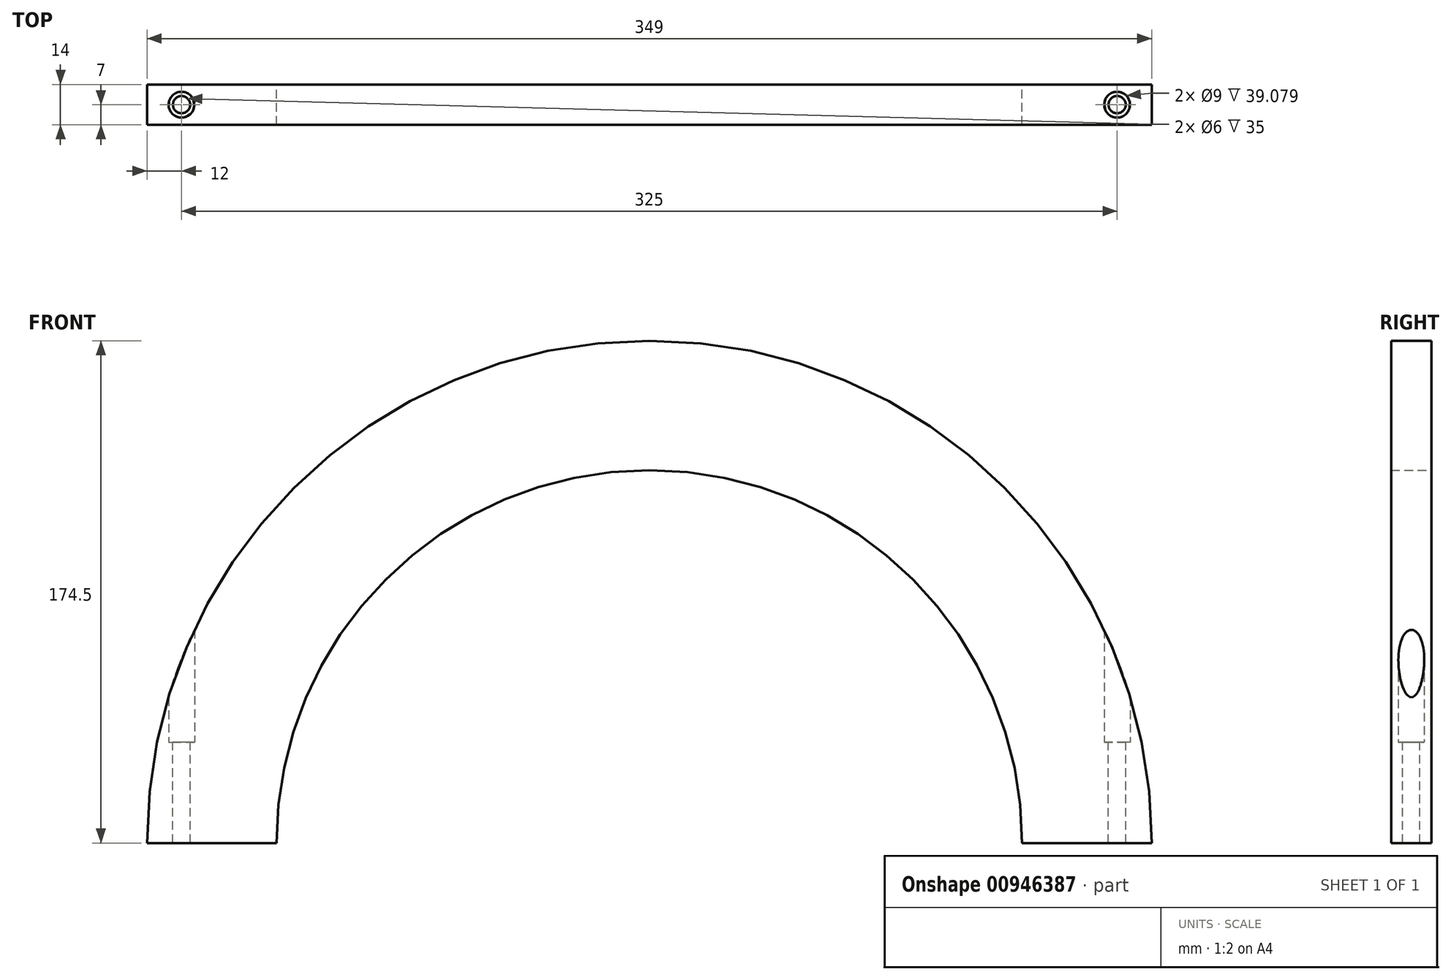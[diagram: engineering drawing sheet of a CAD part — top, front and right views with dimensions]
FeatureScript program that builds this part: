
annotation { "Feature Type Name" : "Feature", "Feature Type Description" : "" }
export const myFeature = defineFeature(function(context is Context, id is Id, definition is map)
    precondition{}
    {
        {
            var Q0;
            Q0=qCreatedBy(makeId("Front.planeOp"),FACE);
            var sketch = newSketch(context, id + "F0", { "sketchPlane" : qUnion([Q0])});
            skArc(sketch, "E0", {"start": v(174.5, 0) * mm, "mid": v(0, 174.5) * mm, "end": v(-174.5, 0) * mm});
            skArc(sketch, "E1", {"start": v(129.5, 0) * mm, "mid": v(0, 129.5) * mm, "end": v(-129.5, 0) * mm});
            skLineSegment(sketch, "E2", {"start": v(-174.5, 0) * mm, "end": v(-129.5, 0) * mm});
            skLineSegment(sketch, "E3.trimOffspring", {"start": v(129.5, 0) * mm, "end": v(174.5, 0) * mm});
            skLineSegment(sketch, "E4", {"start": v(-174.5, 0) * mm, "end": v(-174.5, -52.73) * mm, "construction": true});
            skLineSegment(sketch, "E5", {"start": v(0, 82.24) * mm, "end": v(0, -91.49) * mm, "construction": true});
            skPoint(sketch, "E6.MirrorCS.start.orphan", {"position": v(-174.5, 0) * mm});
            skSolve(sketch);
        }
        {
            var Q0;
            Q0=qSketchRegion(id+"F0",true);
            extrude(context, id + "F1", {"entities" : qUnion([Q0]), "endBound" : BoundingType.SYMMETRIC, "depth" : 14 * mm, "offsetDistance" : 25 * mm});
        }
        {
            var Q0;
            Q0=qSketchRegion(id+"F0",true);
            extrude(context, id + "F2", {"entities" : qUnion([Q0]), "operationType" : NewBodyOperationType.ADD, "endBound" : BoundingType.SYMMETRIC, "depth" : 12 * mm, "offsetDistance" : 25 * mm});
        }
        {
            var Q0;
            Q0=qCreatedBy(makeId("Top.planeOp"),FACE);
            cPlane(context, id + "F3", {"entities" : qUnion([Q0]), "cplaneType" : CPlaneType.OFFSET, "offset" : 55 * mm, "width" : 150 * mm, "height" : 150 * mm});
        }
        {
            var Q0;
            Q0=qCreatedBy(id+"F3.planeOp",FACE);
            var sketch = newSketch(context, id + "F4", { "sketchPlane" : qUnion([Q0])});
            skPoint(sketch, "E7.middle", {"position": v(-162.5, 0) * mm});
            skCircle(sketch, "E8", {"center": v(-162.5, 0) * mm, "radius": 4.5 * mm});
            skLineSegment(sketch, "E9", {"start": v(0, 45.88) * mm, "end": v(0, -42.52) * mm, "construction": true});
            skCircle(sketch, "E10.MirrorC", {"center": v(162.5, 0) * mm, "radius": 4.5 * mm});
            skSolve(sketch);
        }
        {
            var Q0;
            Q0 = qSketchRegion(id + "F4", true);
            extrude(context, id + "F5", {"entities" : qUnion([Q0]), "operationType" : NewBodyOperationType.REMOVE, "endBound" : BoundingType.THROUGH_ALL, "depth" : 25 * mm, "offsetDistance" : 25 * mm});
        }
        {
            var Q0;
            Q0 = qSketchRegion(id + "F4", true);
            extrude(context, id + "F6", {"entities" : qUnion([Q0]), "operationType" : NewBodyOperationType.REMOVE, "oppositeDirection" : true, "depth" : 20 * mm, "offsetDistance" : 25 * mm});
        }
        {
            var Q0;
            Q0=makeQuery(id+"F6.boolean.opBoolean","COPY",FACE,{"derivedFrom":makeQuery(id+"F6.opExtrude","CAP_FACE",FACE,{"disambiguationData":[OSD([sQuery(id+"F4.wireOp",EDGE,"E8")])],"isStart":false})});
            var sketch = newSketch(context, id + "F7", { "sketchPlane" : qUnion([Q0])});
            skCircle(sketch, "E11", {"center": v(-162.5, 0) * mm, "radius": 3 * mm});
            skCircle(sketch, "E12.MirrorC", {"center": v(162.5, 0) * mm, "radius": 3 * mm});
            skSolve(sketch);
        }
        {
            var Q0;
            Q0 = qSketchRegion(id + "F7", true);
            extrude(context, id + "F8", {"entities" : qUnion([Q0]), "operationType" : NewBodyOperationType.REMOVE, "endBound" : BoundingType.THROUGH_ALL, "oppositeDirection" : true, "depth" : 25 * mm, "offsetDistance" : 25 * mm});
        }
    });
